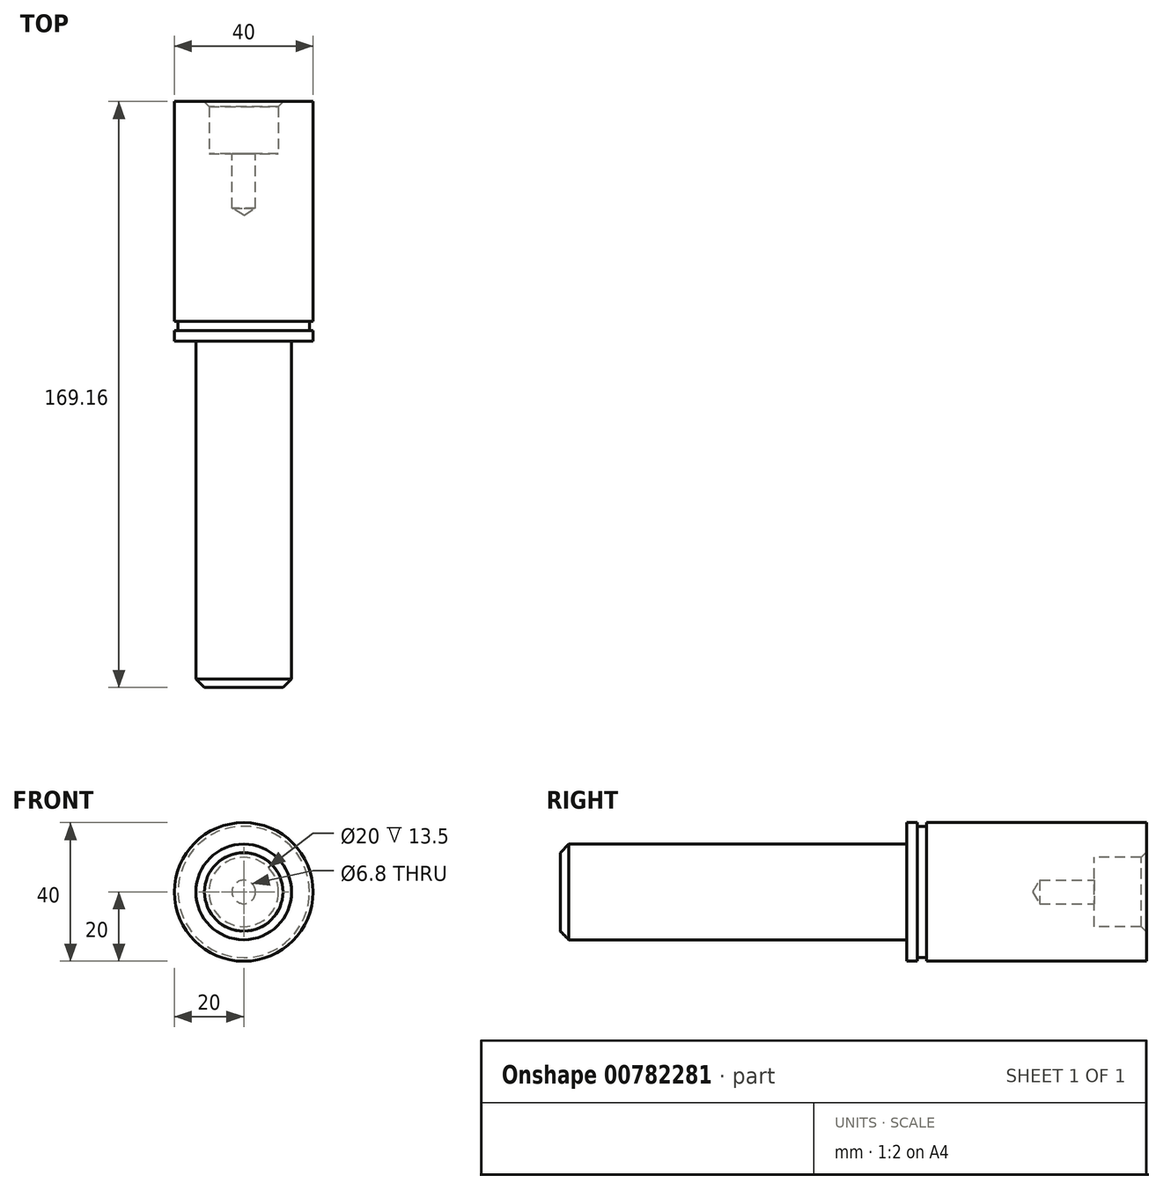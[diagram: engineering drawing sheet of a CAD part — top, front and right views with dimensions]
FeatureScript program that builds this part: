
annotation { "Feature Type Name" : "Feature", "Feature Type Description" : "" }
export const myFeature = defineFeature(function(context is Context, id is Id, definition is map)
    precondition{}
    {
        {
            var Q0;
            Q0=qCreatedBy(makeId("Right.planeOp"),FACE);
            var sketch = newSketch(context, id + "F0", { "sketchPlane" : qUnion([Q0])});
            skLineSegment(sketch, "E0", {"start": v(-77.08, 0) * mm, "end": v(77.08, 0) * mm});
            skLineSegment(sketch, "E1", {"start": v(-77.08, 0) * mm, "end": v(-77.08, 13.8) * mm});
            skLineSegment(sketch, "E2", {"start": v(-77.08, 13.8) * mm, "end": v(22.93, 13.8) * mm});
            skLineSegment(sketch, "E3", {"start": v(22.93, 13.8) * mm, "end": v(22.93, 20) * mm});
            skLineSegment(sketch, "E4", {"start": v(22.93, 20) * mm, "end": v(25.93, 20) * mm});
            skLineSegment(sketch, "E5", {"start": v(25.93, 20) * mm, "end": v(25.92, 0) * mm});
            skLineSegment(sketch, "E6", {"start": v(25.93, 20) * mm, "end": v(28.57, 20) * mm, "construction": true});
            skLineSegment(sketch, "E7", {"start": v(28.57, 0) * mm, "end": v(28.57, 18.96) * mm});
            skLineSegment(sketch, "E8", {"start": v(28.57, 18.96) * mm, "end": v(28.57, 20) * mm});
            skLineSegment(sketch, "E9", {"start": v(28.57, 18.96) * mm, "end": v(25.93, 18.96) * mm});
            skLineSegment(sketch, "E10", {"start": v(92.07, 0) * mm, "end": v(92.07, 20) * mm});
            skLineSegment(sketch, "E11", {"start": v(77.07, 0) * mm, "end": v(77.07, 10) * mm});
            skLineSegment(sketch, "E12", {"start": v(77.07, 10) * mm, "end": v(92.07, 10) * mm});
            skLineSegment(sketch, "E13", {"start": v(28.57, 20) * mm, "end": v(92.07, 20) * mm});
            skSolve(sketch);
        }
        {
            var Q0;
            Q0 = qSketchRegion(id + "F0", true);
            var Q1;
            Q1=sQuery(id+"F0.wireOp",EDGE,"E0");
            revolve(context, id + "F1", {"surfaceOperationType" : NewSurfaceOperationType.NEW, "entities" : qUnion([Q0]), "axis" : qUnion([Q1]), "revolveType" : RevolveType.FULL});
        }
        {
            var Q0;
            Q0=makeQuery(id+"F1.opRevolve","SWEPT_EDGE",EDGE,{"disambiguationData":[OSD([sQuery(id+"F0.wireOp",EDGE,"E10"),sQuery(id+"F0.wireOp",EDGE,"E12")])]});
            chamfer(context, id + "F2", {"entities" : qUnion([Q0]), "chamferType" : ChamferType.OFFSET_ANGLE, "width" : 1.5 * mm, "oppositeDirection" : false, "angle" : 45 * degree, "tangentPropagation" : true});
        }
        {
            var Q0;
            Q0=makeQuery(id+"F1.opRevolve","SWEPT_FACE",FACE,{"disambiguationData":[OSD([sQuery(id+"F0.wireOp",EDGE,"E11")])]});
            var sketch = newSketch(context, id + "F3", { "sketchPlane" : qUnion([Q0])});
            skPoint(sketch, "E14", {"position": v(0, 0) * mm});
            skSolve(sketch);
        }
        {
            var Q0;
            Q0=sQuery(id+"F3.wireOp",VERTEX,"E14");
            var Q1;
            Q1=makeQuery(id+"F1.opRevolve","SWEPT_BODY",BODY,{"disambiguationData":[OSD([sQuery(id+"F0.wireOp",EDGE,"E0"),sQuery(id+"F0.wireOp",EDGE,"E1"),sQuery(id+"F0.wireOp",EDGE,"E2"),sQuery(id+"F0.wireOp",EDGE,"E3"),sQuery(id+"F0.wireOp",EDGE,"E4"),sQuery(id+"F0.wireOp",EDGE,"E5"),sQuery(id+"F0.wireOp",EDGE,"E8"),sQuery(id+"F0.wireOp",EDGE,"E9"),sQuery(id+"F0.wireOp",EDGE,"E10"),sQuery(id+"F0.wireOp",EDGE,"E11"),sQuery(id+"F0.wireOp",EDGE,"E12"),sQuery(id+"F0.wireOp",EDGE,"E13")])]});
            hole(context, id + "F4", {"style" : HoleStyle.SIMPLE, "endStyle" : HoleEndStyle.BLIND, "standardTappedOrClearance" : lookupTablePath({ "standard" : "ISO", "engagement" : "75%", "pitch" : "1.25 mm", "size" : "M8", "type" : "Tapped" }), "standardBlindInLast" : lookupTablePath({ "standard" : "ISO", "engagement" : "75%", "pitch" : "1.25 mm", "size" : "M8", "type" : "Tapped" }), "holeDiameter" : 6.8 * mm, "majorDiameter" : 8 * mm, "showTappedDepth" : true, "holeDepth" : 15.75 * mm, "isTappedThrough" : true, "tappedDepth" : 12 * mm, "tapClearance" : 3, "startFromSketch" : true, "locations" : qUnion([Q0]), "scope" : qUnion([Q1])});
        }
        {
            var Q0;
            Q0=makeQuery(id+"F1.opRevolve","SWEPT_EDGE",EDGE,{"disambiguationData":[OSD([sQuery(id+"F0.wireOp",EDGE,"E1"),sQuery(id+"F0.wireOp",EDGE,"E2")])]});
            chamfer(context, id + "F5", {"entities" : qUnion([Q0]), "chamferType" : ChamferType.OFFSET_ANGLE, "width" : 2.5 * mm, "oppositeDirection" : false, "angle" : 45 * degree, "tangentPropagation" : true});
        }
    });
